# Revit family: WaterConditioner_ION_SB25-SB50
name_source: partatom
category: Mechanical Equipment
revit_build: Autodesk Revit 2014 (Build: 20130308_1515(x64)
units: mm (PartAtom-declared; Revit-internal decimal feet)

## types (4) — shared parameters
Assembly Code = D2020300
Density_Water_20_ION = 998.2000 kg/m³
Issue_Date_ION = 01/07/15
Issue_Rev_ION = A
Manufacturer = ION Enterprises
URL = www.scalebuster.com
UnitConvert_Area = 1 m²

## per-type parameters (varying)
| type | Equipment_Dia_ION | Equipment_Length_ION | UnitConvert_PressureFactor | UnitSize | Water_ConnectionDia_ION | Weight_Dry_ION |
| SB50 | 87 mm  [stored 0.285433 ft] | 390 mm  [stored 1.27953 ft] | 520227 | SquareEndBody : SB50 | 50 mm | 9.20 kg |
| SB40 | 69 mm  [stored 0.226378 ft] | 360 mm  [stored 1.1811 ft] | 1429859 | SquareEndBody : SB40 | 40 mm | 5.30 kg |
| SB32 | 63 mm  [stored 0.206693 ft] | 330 mm | 5809270 | SquareEndBody : SB32 | 32 mm | 4.30 kg |
| SB25 | 57 mm | 300 mm | 10419288 | SquareEndBody : SB25 | 25 mm | 3.40 kg |

note: column(s) folded — value = type name in every type: Model

note: [stored X ft] marks values corroborated as IEEE doubles in the binary element streams (Revit-internal decimal feet)

## geometry (parser evidence)
native form markers: Sweep x4
no freeform markers — native parametric forms only
